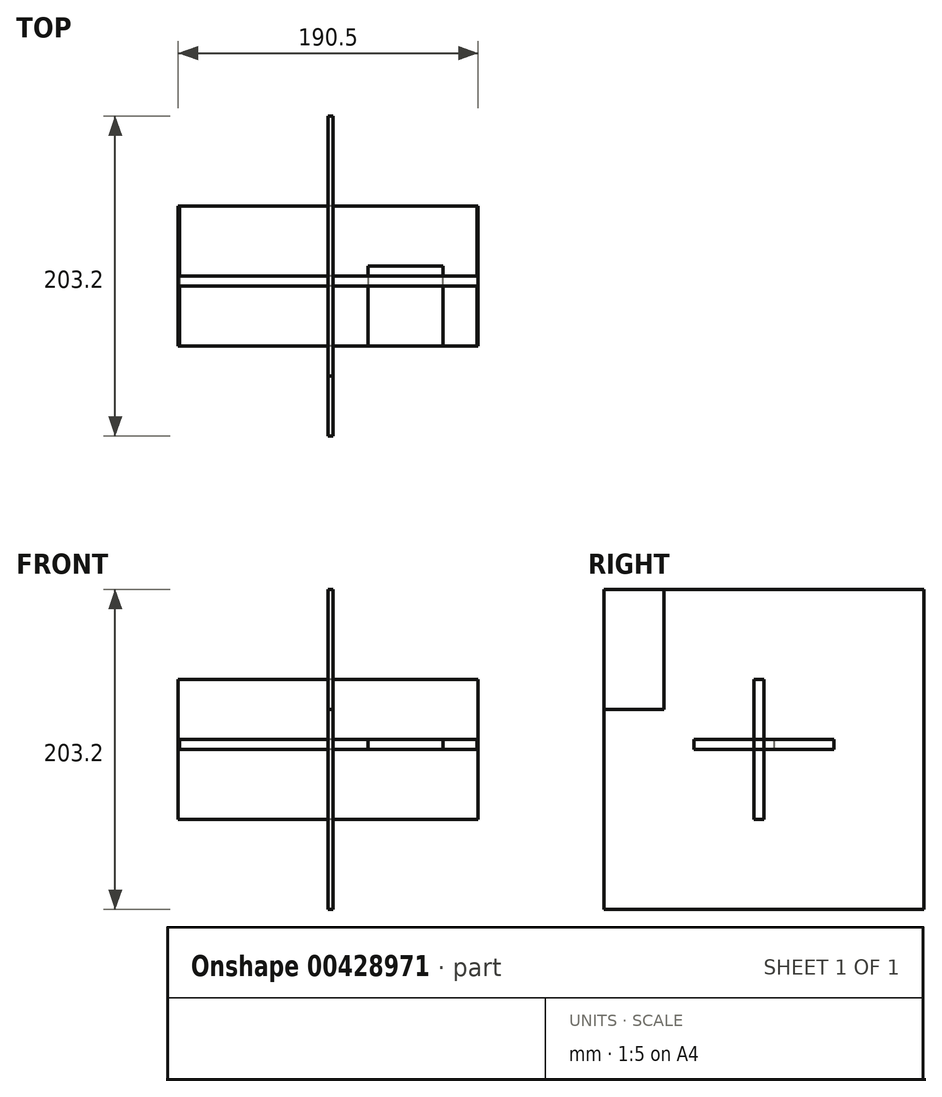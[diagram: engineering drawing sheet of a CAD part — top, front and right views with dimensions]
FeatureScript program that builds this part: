
annotation { "Feature Type Name" : "Feature", "Feature Type Description" : "" }
export const myFeature = defineFeature(function(context is Context, id is Id, definition is map)
    precondition{}
    {
        {
            var Q0;
            Q0=qCreatedBy(makeId("Front.planeOp"),FACE);
            var sketch = newSketch(context, id + "F0", { "sketchPlane" : qUnion([Q0])});
            skLineSegment(sketch, "E0.bottom", {"start": v(95.25, 44.45) * mm, "end": v(-95.25, 44.45) * mm});
            skLineSegment(sketch, "E0.top", {"start": v(95.25, -44.45) * mm, "end": v(-95.25, -44.45) * mm});
            skLineSegment(sketch, "E0.left", {"start": v(95.25, 44.45) * mm, "end": v(95.25, -44.45) * mm});
            skLineSegment(sketch, "E0.right", {"start": v(-95.25, 44.45) * mm, "end": v(-95.25, -44.45) * mm});
            skPoint(sketch, "E0.middle", {"position": v(0, 0) * mm});
            skSolve(sketch);
        }
        {
            var Q0;
            Q0 = qSketchRegion(id + "F0", true);
            extrude(context, id + "F1", {"entities" : qUnion([Q0]), "depth" : 6.35 * mm});
        }
        {
            var Q0;
            Q0=qCreatedBy(makeId("Top.planeOp"),FACE);
            var sketch = newSketch(context, id + "F2", { "sketchPlane" : qUnion([Q0])});
            skLineSegment(sketch, "E1.bottom", {"start": v(95.25, 44.45) * mm, "end": v(-95.25, 44.45) * mm});
            skLineSegment(sketch, "E1.top", {"start": v(95.25, -44.45) * mm, "end": v(73.03, -44.45) * mm});
            skLineSegment(sketch, "E1.left", {"start": v(95.25, 44.45) * mm, "end": v(95.25, -44.45) * mm});
            skLineSegment(sketch, "E1.right", {"start": v(-95.25, 44.45) * mm, "end": v(-95.25, -44.45) * mm});
            skPoint(sketch, "E1.middle", {"position": v(0, 0) * mm});
            skLineSegment(sketch, "E2", {"start": v(73.03, -44.45) * mm, "end": v(73.03, 6.35) * mm});
            skLineSegment(sketch, "E3", {"start": v(73.03, 6.35) * mm, "end": v(25.4, 6.35) * mm});
            skLineSegment(sketch, "E4", {"start": v(25.4, 6.35) * mm, "end": v(25.4, -44.45) * mm});
            skLineSegment(sketch, "E5.trimOffspring", {"start": v(25.4, -44.45) * mm, "end": v(-95.25, -44.45) * mm});
            skSolve(sketch);
        }
        {
            var Q0;
            Q0 = qSketchRegion(id + "F2", true);
            extrude(context, id + "F3", {"entities" : qUnion([Q0]), "depth" : 6.35 * mm});
        }
        {
            var Q0;
            Q0=qCreatedBy(makeId("Top.planeOp"),FACE);
            var sketch = newSketch(context, id + "F4", { "sketchPlane" : qUnion([Q0])});
            skLineSegment(sketch, "E6.bottom", {"start": v(94.46, 44.45) * mm, "end": v(-94.46, 44.45) * mm});
            skLineSegment(sketch, "E6.top", {"start": v(94.46, -44.45) * mm, "end": v(-94.46, -44.45) * mm});
            skLineSegment(sketch, "E6.left", {"start": v(94.46, 44.45) * mm, "end": v(94.46, -44.45) * mm});
            skLineSegment(sketch, "E6.right", {"start": v(-94.46, 44.45) * mm, "end": v(-94.46, -44.45) * mm});
            skPoint(sketch, "E6.middle", {"position": v(0, 0) * mm});
            skSolve(sketch);
        }
        {
            var Q0;
            Q0 = qSketchRegion(id + "F4", true);
            extrude(context, id + "F5", {"entities" : qUnion([Q0]), "depth" : 6.35 * mm});
        }
        {
            var Q0;
            Q0=qCreatedBy(makeId("Right.planeOp"),FACE);
            var sketch = newSketch(context, id + "F6", { "sketchPlane" : qUnion([Q0])});
            skLineSegment(sketch, "E7.bottom", {"start": v(-101.6, -101.6) * mm, "end": v(101.6, -101.6) * mm});
            skLineSegment(sketch, "E7.top", {"start": v(-101.6, 101.6) * mm, "end": v(101.6, 101.6) * mm});
            skLineSegment(sketch, "E7.left", {"start": v(-101.6, -101.6) * mm, "end": v(-101.6, 101.6) * mm});
            skLineSegment(sketch, "E7.right", {"start": v(101.6, -101.6) * mm, "end": v(101.6, 101.6) * mm});
            skPoint(sketch, "E7.middle", {"position": v(0, 0) * mm});
            skSolve(sketch);
        }
        {
            var Q0;
            Q0 = qSketchRegion(id + "F6", true);
            extrude(context, id + "F7", {"entities" : qUnion([Q0]), "depth" : 3.17 * mm});
        }
        {
            var Q0;
            Q0=qCreatedBy(makeId("Right.planeOp"),FACE);
            var sketch = newSketch(context, id + "F8", { "sketchPlane" : qUnion([Q0])});
            skLineSegment(sketch, "E8.bottom", {"start": v(-101.6, -101.6) * mm, "end": v(101.6, -101.6) * mm});
            skLineSegment(sketch, "E8.top", {"start": v(-101.6, 101.6) * mm, "end": v(101.6, 101.6) * mm, "construction": true});
            skLineSegment(sketch, "E8.left", {"start": v(-101.6, -101.6) * mm, "end": v(-101.6, 101.6) * mm, "construction": true});
            skLineSegment(sketch, "E8.right", {"start": v(101.6, -101.6) * mm, "end": v(101.6, 101.6) * mm});
            skPoint(sketch, "E8.middle", {"position": v(0, 0) * mm});
            skLineSegment(sketch, "E9", {"start": v(-63.5, 101.6) * mm, "end": v(-63.5, 25.4) * mm});
            skLineSegment(sketch, "E10", {"start": v(-63.5, 25.4) * mm, "end": v(-101.6, 25.4) * mm});
            skLineSegment(sketch, "E11", {"start": v(-63.5, 101.6) * mm, "end": v(101.6, 101.6) * mm});
            skLineSegment(sketch, "E12", {"start": v(-101.6, -101.6) * mm, "end": v(-101.6, 25.4) * mm, "construction": true});
            skLineSegment(sketch, "E13", {"start": v(-101.6, 25.4) * mm, "end": v(-101.6, -101.6) * mm});
            skSolve(sketch);
        }
        {
            var Q0;
            Q0 = qSketchRegion(id + "F8", true);
            extrude(context, id + "F9", {"entities" : qUnion([Q0]), "depth" : 3.17 * mm});
        }
    });
